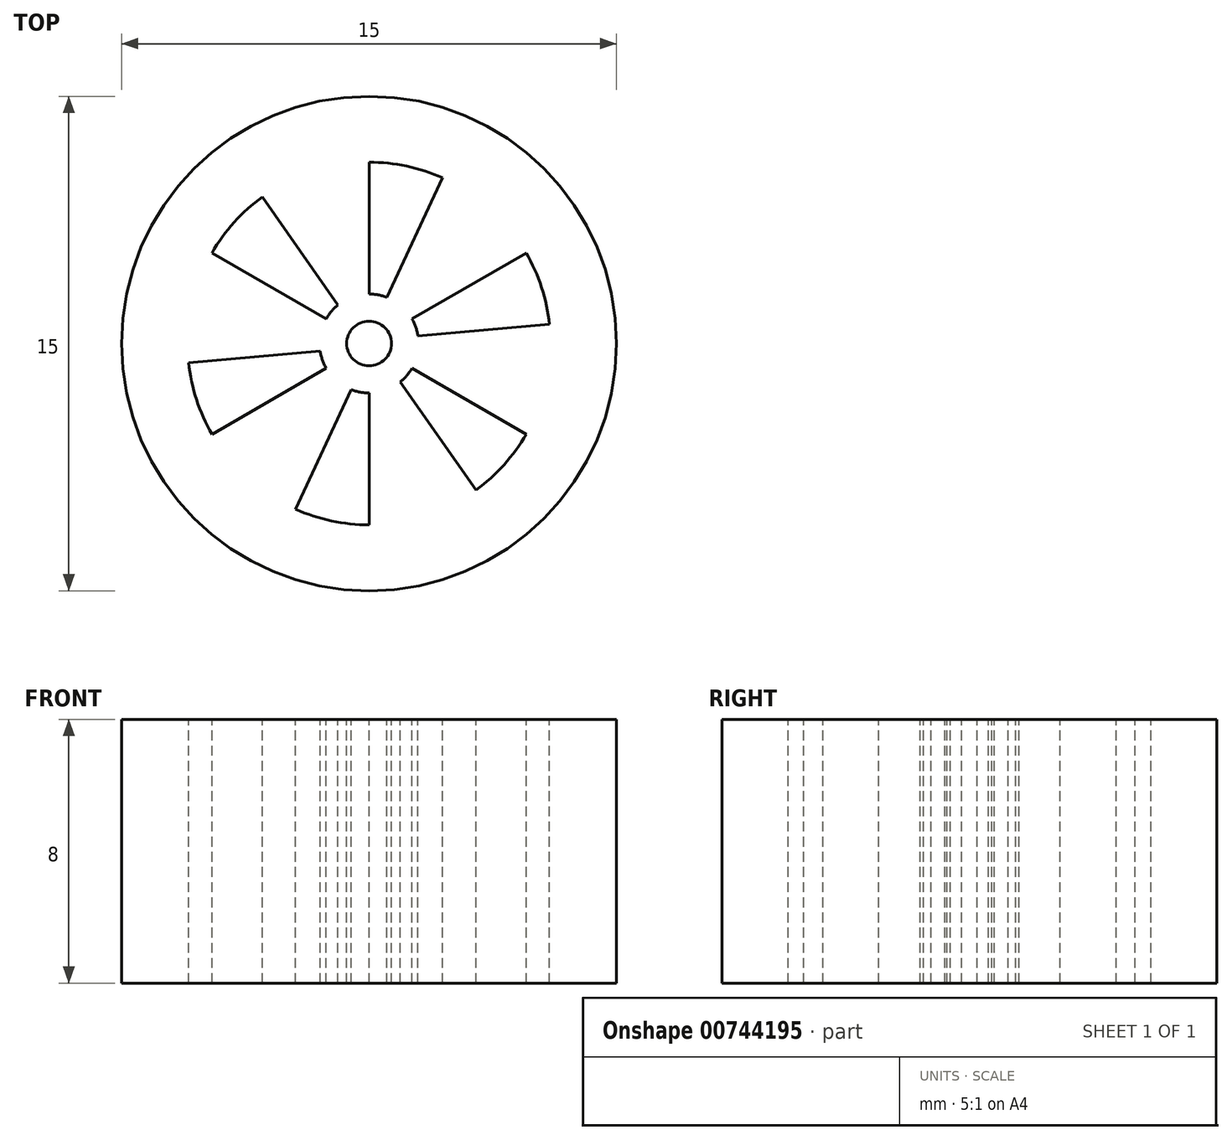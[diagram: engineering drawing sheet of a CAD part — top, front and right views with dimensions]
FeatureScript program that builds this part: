
annotation { "Feature Type Name" : "Feature", "Feature Type Description" : "" }
export const myFeature = defineFeature(function(context is Context, id is Id, definition is map)
    precondition{}
    {
        {
            var Q0;
            Q0=qCreatedBy(makeId("Top.planeOp"),FACE);
            var sketch = newSketch(context, id + "F0", { "sketchPlane" : qUnion([Q0])});
            skCircle(sketch, "E0", {"center": v(0, 0) * mm, "radius": 7.5 * mm});
            skSolve(sketch);
        }
        {
            var Q0;
            Q0=makeQuery(id+"F0.imprint","IMPRINT",FACE,{"disambiguationData":[TD([[makeQuery(id+"F0.imprint","IMPRINT",EDGE,{"derivedFrom":sQuery(id+"F0.wireOp",EDGE,"E0")}),1.0]])]});
            extrude(context, id + "F1", {"entities" : qUnion([Q0]), "depth" : 8 * mm, "offsetDistance" : 25 * mm});
        }
        {
            var Q0;
            Q0=makeQuery(id+"F1.opExtrude","CAP_FACE",FACE,{"disambiguationData":[OSD([sQuery(id+"F0.wireOp",EDGE,"E0")])],"isStart":false});
            var sketch = newSketch(context, id + "F2", { "sketchPlane" : qUnion([Q0])});
            skCircle(sketch, "E1", {"center": v(0, 0) * mm, "radius": 1.5 * mm});
            skCircle(sketch, "E2", {"center": v(0, 0) * mm, "radius": 5.5 * mm});
            skLineSegment(sketch, "E3", {"start": v(0, 1.5) * mm, "end": v(0, 5.5) * mm});
            skLineSegment(sketch, "E4", {"start": v(0.54, 1.4) * mm, "end": v(2.23, 5.03) * mm});
            skLineSegment(sketch, "E5.1.0", {"start": v(-0.94, 1.17) * mm, "end": v(-3.24, 4.45) * mm});
            skLineSegment(sketch, "E5.1.1", {"start": v(-1.3, 0.75) * mm, "end": v(-4.76, 2.75) * mm});
            skLineSegment(sketch, "E5.2.0", {"start": v(-1.48, -0.23) * mm, "end": v(-5.47, -0.58) * mm});
            skLineSegment(sketch, "E5.2.1", {"start": v(-1.3, -0.75) * mm, "end": v(-4.76, -2.75) * mm});
            skLineSegment(sketch, "E5.3.0", {"start": v(-0.54, -1.4) * mm, "end": v(-2.23, -5.03) * mm});
            skLineSegment(sketch, "E5.3.1", {"start": v(0, -1.5) * mm, "end": v(0, -5.5) * mm});
            skLineSegment(sketch, "E5.4.0", {"start": v(0.94, -1.17) * mm, "end": v(3.24, -4.45) * mm});
            skLineSegment(sketch, "E5.4.1", {"start": v(1.3, -0.75) * mm, "end": v(4.76, -2.75) * mm});
            skLineSegment(sketch, "E5.5.0", {"start": v(1.48, 0.23) * mm, "end": v(5.47, 0.58) * mm});
            skLineSegment(sketch, "E5.5.1", {"start": v(1.3, 0.75) * mm, "end": v(4.76, 2.75) * mm});
            skSolve(sketch);
        }
        {
            var Q0;
            {var subQ0=sQuery(id+"F2.wireOp",EDGE,"E3");Q0=makeQuery(id+"F2.imprint","IMPRINT",FACE,{"disambiguationData":[TD([[makeQuery(id+"F2.imprint","IMPRINT",EDGE,{"derivedFrom":subQ0}),-1.0]])]});}
            var Q1;
            {var subQ0=sQuery(id+"F2.wireOp",EDGE,"E5.1.0");Q1=makeQuery(id+"F2.imprint","IMPRINT",FACE,{"disambiguationData":[TD([[makeQuery(id+"F2.imprint","IMPRINT",EDGE,{"derivedFrom":subQ0}),1.0]])]});}
            var Q2;
            {var subQ0=sQuery(id+"F2.wireOp",EDGE,"E5.2.0");Q2=makeQuery(id+"F2.imprint","IMPRINT",FACE,{"disambiguationData":[TD([[makeQuery(id+"F2.imprint","IMPRINT",EDGE,{"derivedFrom":subQ0}),1.0]])]});}
            var Q3;
            {var subQ0=sQuery(id+"F2.wireOp",EDGE,"E5.3.0");Q3=makeQuery(id+"F2.imprint","IMPRINT",FACE,{"disambiguationData":[TD([[makeQuery(id+"F2.imprint","IMPRINT",EDGE,{"derivedFrom":subQ0}),1.0]])]});}
            var Q4;
            {var subQ0=sQuery(id+"F2.wireOp",EDGE,"E5.4.0");Q4=makeQuery(id+"F2.imprint","IMPRINT",FACE,{"disambiguationData":[TD([[makeQuery(id+"F2.imprint","IMPRINT",EDGE,{"derivedFrom":subQ0}),1.0]])]});}
            var Q5;
            {var subQ0=sQuery(id+"F2.wireOp",EDGE,"E5.5.0");Q5=makeQuery(id+"F2.imprint","IMPRINT",FACE,{"disambiguationData":[TD([[makeQuery(id+"F2.imprint","IMPRINT",EDGE,{"derivedFrom":subQ0}),1.0]])]});}
            extrude(context, id + "F3", {"entities" : qUnion([Q0, Q1, Q2, Q3, Q4, Q5]), "operationType" : NewBodyOperationType.REMOVE, "oppositeDirection" : true, "depth" : 100 * mm, "offsetDistance" : 25 * mm});
        }
        {
            var Q0;
            Q0=makeQuery(id+"F1.opExtrude","CAP_FACE",FACE,{"disambiguationData":[OSD([sQuery(id+"F0.wireOp",EDGE,"E0")])],"isStart":false});
            var sketch = newSketch(context, id + "F4", { "sketchPlane" : qUnion([Q0])});
            skCircle(sketch, "E6", {"center": v(0, 0) * mm, "radius": 0.68 * mm});
            skSolve(sketch);
        }
        {
            var Q0;
            Q0=makeQuery(id+"F4.imprint","IMPRINT",FACE,{"disambiguationData":[TD([[makeQuery(id+"F4.imprint","IMPRINT",EDGE,{"derivedFrom":sQuery(id+"F4.wireOp",EDGE,"E6")}),1.0]])]});
            extrude(context, id + "F5", {"entities" : qUnion([Q0]), "operationType" : NewBodyOperationType.REMOVE, "oppositeDirection" : true, "depth" : 100 * mm, "offsetDistance" : 25 * mm});
        }
    });
